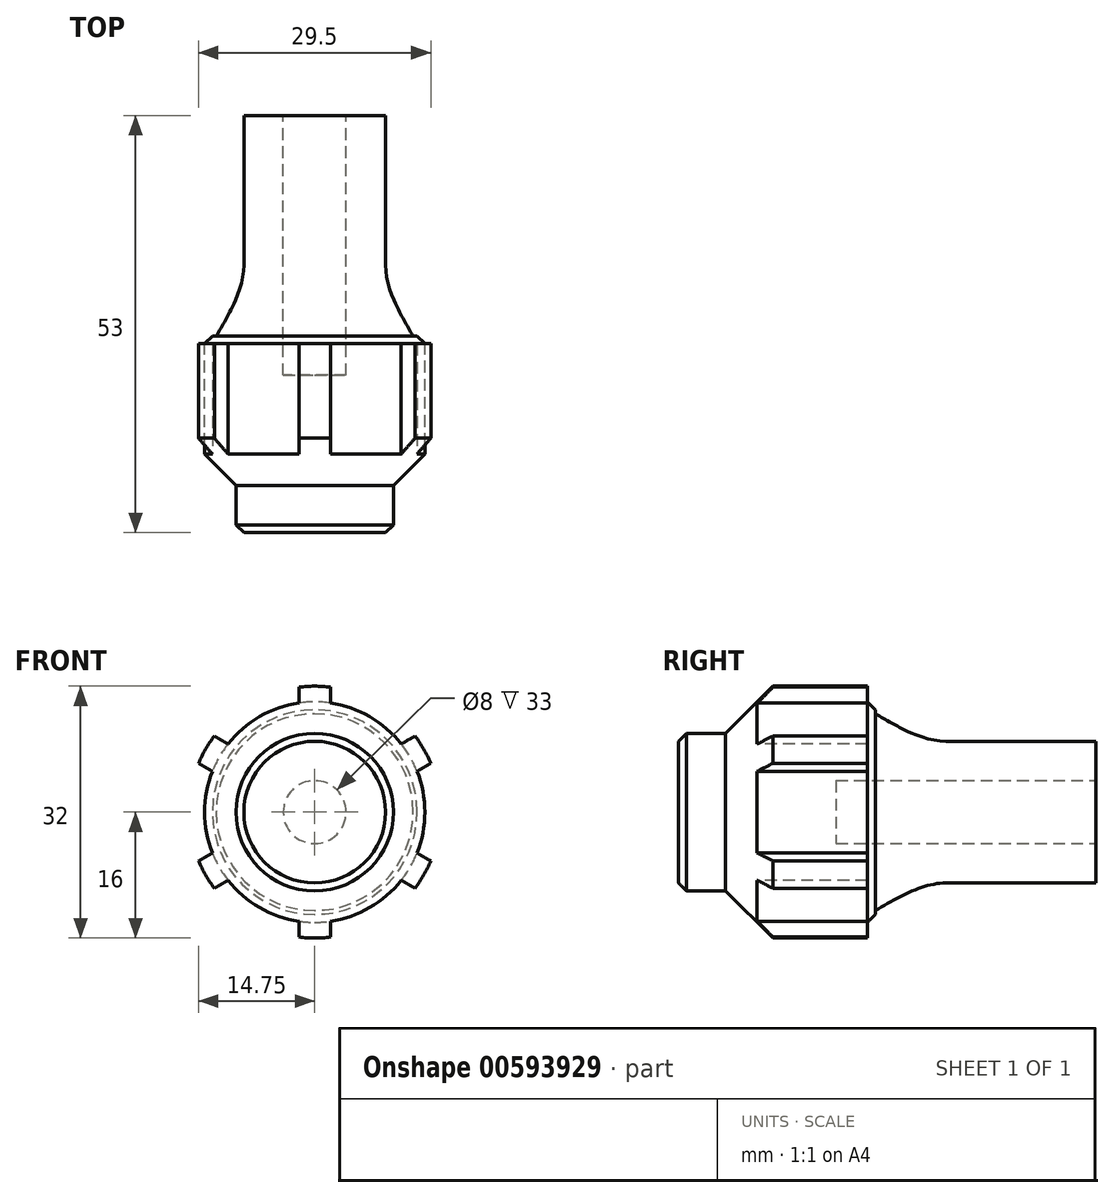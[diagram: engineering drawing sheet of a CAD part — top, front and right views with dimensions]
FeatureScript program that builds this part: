
annotation { "Feature Type Name" : "Feature", "Feature Type Description" : "" }
export const myFeature = defineFeature(function(context is Context, id is Id, definition is map)
    precondition{}
    {
        {
            var Q0;
            Q0=qCreatedBy(makeId("Front.planeOp"),FACE);
            var sketch = newSketch(context, id + "F0", { "sketchPlane" : qUnion([Q0])});
            skCircle(sketch, "E0", {"center": v(0, 0) * mm, "radius": 9 * mm});
            skSolve(sketch);
        }
        {
            var Q0;
            Q0=makeQuery(id+"F0.imprint","IMPRINT",FACE,{"disambiguationData":[TD([[makeQuery(id+"F0.imprint","IMPRINT",EDGE,{"derivedFrom":sQuery(id+"F0.wireOp",EDGE,"E0")}),1.0]])]});
            extrude(context, id + "F1", {"entities" : qUnion([Q0]), "depth" : 19 * mm, "offsetDistance" : 25 * mm});
        }
        {
            var Q0;
            Q0=makeQuery(id+"F1.opExtrude","CAP_FACE",FACE,{"disambiguationData":[OSD([sQuery(id+"F0.wireOp",EDGE,"E0")])],"isStart":false});
            cPlane(context, id + "F2", {"entities" : qUnion([Q0]), "cplaneType" : CPlaneType.OFFSET, "offset" : 9 * mm, "width" : 150 * mm, "height" : 150 * mm});
        }
        {
            var Q0;
            Q0=qCreatedBy(id+"F2.planeOp",FACE);
            var sketch = newSketch(context, id + "F3", { "sketchPlane" : qUnion([Q0])});
            skCircle(sketch, "E1", {"center": v(0, 0) * mm, "radius": 12.5 * mm});
            skSolve(sketch);
        }
        {
            var Q0;
            Q0=makeQuery(id+"F1.opExtrude","CAP_FACE",FACE,{"disambiguationData":[OSD([sQuery(id+"F0.wireOp",EDGE,"E0")])],"isStart":true});
            var sketch = newSketch(context, id + "F4", { "sketchPlane" : qUnion([Q0])});
            skCircle(sketch, "E2", {"center": v(0, 0) * mm, "radius": 4 * mm});
            skSolve(sketch);
        }
        {
            var Q1;
            Q1=makeQuery(id+"F1.opExtrude","CAP_FACE",FACE,{"disambiguationData":[OSD([sQuery(id+"F0.wireOp",EDGE,"E0")])],"isStart":false});
            var Q2;
            Q2=makeQuery(id+"F3.imprint","IMPRINT",FACE,{"disambiguationData":[TD([[makeQuery(id+"F3.imprint","IMPRINT",EDGE,{"derivedFrom":sQuery(id+"F3.wireOp",EDGE,"E1")}),1.0]])]});
            loft(context, id + "F5", {"operationType" : NewBodyOperationType.ADD, "startCondition" : LoftEndDerivativeType.NORMAL_TO_PROFILE, "startMagnitude" : 1, "sheetProfilesArray" : [{ "sheetProfileEntities" : qUnion([Q1]) }, { "sheetProfileEntities" : qUnion([Q2]) }]});
        }
        {
            var Q0;
            Q0=makeQuery(id+"F5.opLoft","CAP_FACE",FACE,{"disambiguationData":[OSD([makeQuery(id+"F3.imprint","IMPRINT",FACE,{"disambiguationData":[TD([[makeQuery(id+"F3.imprint","IMPRINT",EDGE,{"derivedFrom":sQuery(id+"F3.wireOp",EDGE,"E1")}),1.0]])]})])],"isStart":true});
            var sketch = newSketch(context, id + "F6", { "sketchPlane" : qUnion([Q0])});
            skCircle(sketch, "E3", {"center": v(0, 0) * mm, "radius": 14 * mm});
            skSolve(sketch);
        }
        {
            var Q0;
            Q0=makeQuery(id+"F6.imprint","IMPRINT",FACE,{"disambiguationData":[TD([[makeQuery(id+"F6.imprint","IMPRINT",EDGE,{"derivedFrom":makeQuery(id+"F5.opLoft","MID_CAP_EDGE",EDGE,{"disambiguationData":[OSD([sQuery(id+"F0.wireOp",EDGE,"E0"),sQuery(id+"F3.wireOp",EDGE,"E1")])],"capPos":1.0})}),1.0]])]});
            var Q1;
            Q1=makeQuery(id+"F6.imprint","IMPRINT",FACE,{"disambiguationData":[TD([[makeQuery(id+"F6.imprint","IMPRINT",EDGE,{"derivedFrom":sQuery(id+"F6.wireOp",EDGE,"E3")}),1.0]])]});
            extrude(context, id + "F7", {"entities" : qUnion([Q0, Q1]), "operationType" : NewBodyOperationType.ADD, "depth" : 19 * mm, "offsetDistance" : 25 * mm});
        }
        {
            var Q0;
            Q0=makeQuery(id+"F7.opExtrude","CAP_FACE",FACE,{"disambiguationData":[OSD([sQuery(id+"F6.wireOp",EDGE,"E3")])],"isStart":false});
            var sketch = newSketch(context, id + "F8", { "sketchPlane" : qUnion([Q0])});
            skCircle(sketch, "E4", {"center": v(0, 0) * mm, "radius": 10 * mm});
            skSolve(sketch);
        }
        {
            var Q0;
            Q0 = qSketchRegion(id + "F8", true);
            extrude(context, id + "F9", {"entities" : qUnion([Q0]), "operationType" : NewBodyOperationType.ADD, "depth" : 6 * mm, "offsetDistance" : 25 * mm});
        }
        {
            var Q0;
            Q0=makeQuery(id+"F7.opExtrude","CAP_EDGE",EDGE,{"disambiguationData":[OSD([sQuery(id+"F6.wireOp",EDGE,"E3")])],"isStart":false});
            chamfer(context, id + "F10", {"entities" : qUnion([Q0]), "width" : 4 * mm, "tangentPropagation" : true});
        }
        {
            var Q0;
            Q0=makeQuery(id+"F7.opExtrude","CAP_EDGE",EDGE,{"disambiguationData":[OSD([sQuery(id+"F6.wireOp",EDGE,"E3")])],"isStart":true});
            var Q1;
            Q1=makeQuery(id+"F9.opExtrude","CAP_EDGE",EDGE,{"disambiguationData":[OSD([sQuery(id+"F8.wireOp",EDGE,"E4")])],"isStart":false});
            chamfer(context, id + "F11", {"entities" : qUnion([Q0, Q1]), "width" : 1 * mm, "tangentPropagation" : true});
        }
        {
            var Q0;
            Q0=qCreatedBy(makeId("Front.planeOp"),FACE);
            cPlane(context, id + "F12", {"entities" : qUnion([Q0]), "cplaneType" : CPlaneType.OFFSET, "offset" : 43 * mm, "width" : 150 * mm, "height" : 150 * mm});
        }
        {
            var Q0;
            Q0=qCreatedBy(id+"F12.planeOp",FACE);
            var sketch = newSketch(context, id + "F13", { "sketchPlane" : qUnion([Q0])});
            skArc(sketch, "E5.0", {"start": v(2, 13.86) * mm, "mid": v(0, 14) * mm, "end": v(-2, 13.86) * mm});
            skLineSegment(sketch, "E6", {"start": v(-2, 13.86) * mm, "end": v(-2, 15.87) * mm});
            skLineSegment(sketch, "E7.MirrorCS", {"start": v(2, 13.86) * mm, "end": v(2, 15.87) * mm});
            skArc(sketch, "E8", {"start": v(-2, 15.87) * mm, "mid": v(0, 16) * mm, "end": v(2, 15.87) * mm});
            skArc(sketch, "E9.1.0", {"start": v(-11, 8.66) * mm, "mid": v(-12.12, 7) * mm, "end": v(-13, 5.2) * mm});
            skLineSegment(sketch, "E9.1.1", {"start": v(-11, 8.66) * mm, "end": v(-12.75, 9.67) * mm});
            skArc(sketch, "E9.1.2", {"start": v(-14.75, 6.2) * mm, "mid": v(-13.86, 8) * mm, "end": v(-12.75, 9.67) * mm});
            skLineSegment(sketch, "E9.1.3", {"start": v(-13, 5.2) * mm, "end": v(-14.75, 6.2) * mm});
            skArc(sketch, "E9.2.0", {"start": v(-13, -5.2) * mm, "mid": v(-12.12, -7) * mm, "end": v(-11, -8.66) * mm});
            skLineSegment(sketch, "E9.2.1", {"start": v(-13, -5.2) * mm, "end": v(-14.75, -6.2) * mm});
            skArc(sketch, "E9.2.2", {"start": v(-12.75, -9.67) * mm, "mid": v(-13.86, -8) * mm, "end": v(-14.75, -6.2) * mm});
            skLineSegment(sketch, "E9.2.3", {"start": v(-11, -8.66) * mm, "end": v(-12.75, -9.67) * mm});
            skArc(sketch, "E9.3.0", {"start": v(-2, -13.86) * mm, "mid": v(0, -14) * mm, "end": v(2, -13.86) * mm});
            skLineSegment(sketch, "E9.3.1", {"start": v(-2, -13.86) * mm, "end": v(-2, -15.87) * mm});
            skArc(sketch, "E9.3.2", {"start": v(2, -15.87) * mm, "mid": v(0, -16) * mm, "end": v(-2, -15.87) * mm});
            skLineSegment(sketch, "E9.3.3", {"start": v(2, -13.86) * mm, "end": v(2, -15.87) * mm});
            skArc(sketch, "E9.4.0", {"start": v(11, -8.66) * mm, "mid": v(12.12, -7) * mm, "end": v(13, -5.2) * mm});
            skLineSegment(sketch, "E9.4.1", {"start": v(11, -8.66) * mm, "end": v(12.75, -9.67) * mm});
            skArc(sketch, "E9.4.2", {"start": v(14.75, -6.2) * mm, "mid": v(13.86, -8) * mm, "end": v(12.75, -9.67) * mm});
            skLineSegment(sketch, "E9.4.3", {"start": v(13, -5.2) * mm, "end": v(14.75, -6.2) * mm});
            skArc(sketch, "E9.5.0", {"start": v(13, 5.2) * mm, "mid": v(12.12, 7) * mm, "end": v(11, 8.66) * mm});
            skLineSegment(sketch, "E9.5.1", {"start": v(13, 5.2) * mm, "end": v(14.75, 6.2) * mm});
            skArc(sketch, "E9.5.2", {"start": v(12.75, 9.67) * mm, "mid": v(13.86, 8) * mm, "end": v(14.75, 6.2) * mm});
            skLineSegment(sketch, "E9.5.3", {"start": v(11, 8.66) * mm, "end": v(12.75, 9.67) * mm});
            skSolve(sketch);
        }
        {
            var Q0;
            Q0=makeQuery(id+"F13.imprint","IMPRINT",FACE,{"disambiguationData":[TD([[makeQuery(id+"F13.imprint","IMPRINT",EDGE,{"derivedFrom":sQuery(id+"F13.wireOp",EDGE,"E5.0")}),-1.0]])]});
            var Q1;
            Q1=makeQuery(id+"F13.imprint","IMPRINT",FACE,{"disambiguationData":[TD([[makeQuery(id+"F13.imprint","IMPRINT",EDGE,{"derivedFrom":sQuery(id+"F13.wireOp",EDGE,"E9.1.0")}),-1.0]])]});
            var Q2;
            Q2=makeQuery(id+"F13.imprint","IMPRINT",FACE,{"disambiguationData":[TD([[makeQuery(id+"F13.imprint","IMPRINT",EDGE,{"derivedFrom":sQuery(id+"F13.wireOp",EDGE,"E9.2.0")}),-1.0]])]});
            var Q3;
            Q3=makeQuery(id+"F13.imprint","IMPRINT",FACE,{"disambiguationData":[TD([[makeQuery(id+"F13.imprint","IMPRINT",EDGE,{"derivedFrom":sQuery(id+"F13.wireOp",EDGE,"E9.4.0")}),-1.0]])]});
            var Q4;
            Q4=makeQuery(id+"F13.imprint","IMPRINT",FACE,{"disambiguationData":[TD([[makeQuery(id+"F13.imprint","IMPRINT",EDGE,{"derivedFrom":sQuery(id+"F13.wireOp",EDGE,"E9.5.0")}),-1.0]])]});
            var Q5;
            Q5=makeQuery(id+"F13.imprint","IMPRINT",FACE,{"disambiguationData":[TD([[makeQuery(id+"F13.imprint","IMPRINT",EDGE,{"derivedFrom":sQuery(id+"F13.wireOp",EDGE,"E9.5.0")}),-1.0]])]});
            var Q6;
            Q6=makeQuery(id+"F13.imprint","IMPRINT",FACE,{"disambiguationData":[TD([[makeQuery(id+"F13.imprint","IMPRINT",EDGE,{"derivedFrom":sQuery(id+"F13.wireOp",EDGE,"E9.3.0")}),-1.0]])]});
            var Q7;
            Q7=makeQuery(id+"F7.opExtrude","CAP_FACE",FACE,{"disambiguationData":[OSD([sQuery(id+"F6.wireOp",EDGE,"E3")])],"isStart":true});
            extrude(context, id + "F14", {"entities" : qUnion([Q0, Q1, Q2, Q3, Q4, Q5, Q6]), "operationType" : NewBodyOperationType.ADD, "endBound" : BoundingType.UP_TO_SURFACE, "oppositeDirection" : true, "depth" : 25 * mm, "endBoundEntityFace" : qUnion([Q7]), "hasOffset" : true, "offsetDistance" : 1 * mm});
        }
        {
            var Q0;
            Q0=makeQuery(id+"F14.opExtrude","CAP_EDGE",EDGE,{"disambiguationData":[OSD([sQuery(id+"F13.wireOp",EDGE,"E9.1.2")])],"isStart":true});
            var Q1;
            Q1=makeQuery(id+"F14.opExtrude","CAP_EDGE",EDGE,{"disambiguationData":[OSD([sQuery(id+"F13.wireOp",EDGE,"E9.2.2")])],"isStart":true});
            var Q2;
            Q2=makeQuery(id+"F14.opExtrude","CAP_EDGE",EDGE,{"disambiguationData":[OSD([sQuery(id+"F13.wireOp",EDGE,"E8")])],"isStart":true});
            var Q3;
            Q3=makeQuery(id+"F14.opExtrude","CAP_EDGE",EDGE,{"disambiguationData":[OSD([sQuery(id+"F13.wireOp",EDGE,"E9.5.2")])],"isStart":true});
            var Q4;
            Q4=makeQuery(id+"F14.opExtrude","CAP_EDGE",EDGE,{"disambiguationData":[OSD([sQuery(id+"F13.wireOp",EDGE,"E9.4.2")])],"isStart":true});
            var Q5;
            Q5=makeQuery(id+"F14.opExtrude","CAP_EDGE",EDGE,{"disambiguationData":[OSD([sQuery(id+"F13.wireOp",EDGE,"E9.3.2")])],"isStart":true});
            var Q6;
            Q6=makeQuery(id+"F14.opExtrude","TWEAK_EDGE",EDGE,{"derivedFrom":[makeQuery(id+"F7.opExtrude","CAP_FACE",FACE,{"disambiguationData":[OSD([sQuery(id+"F6.wireOp",EDGE,"E3")])],"isStart":true}),makeQuery(id+"F13.imprint","IMPRINT",EDGE,{"derivedFrom":sQuery(id+"F13.wireOp",EDGE,"E8")})]});
            var Q7;
            Q7=makeQuery(id+"F14.opExtrude","TWEAK_EDGE",EDGE,{"derivedFrom":[makeQuery(id+"F7.opExtrude","CAP_FACE",FACE,{"disambiguationData":[OSD([sQuery(id+"F6.wireOp",EDGE,"E3")])],"isStart":true}),makeQuery(id+"F13.imprint","IMPRINT",EDGE,{"derivedFrom":sQuery(id+"F13.wireOp",EDGE,"E9.5.2")})]});
            var Q8;
            Q8=makeQuery(id+"F14.opExtrude","TWEAK_EDGE",EDGE,{"derivedFrom":[makeQuery(id+"F7.opExtrude","CAP_FACE",FACE,{"disambiguationData":[OSD([sQuery(id+"F6.wireOp",EDGE,"E3")])],"isStart":true}),makeQuery(id+"F13.imprint","IMPRINT",EDGE,{"derivedFrom":sQuery(id+"F13.wireOp",EDGE,"E9.1.2")})]});
            var Q9;
            Q9=makeQuery(id+"F14.opExtrude","TWEAK_EDGE",EDGE,{"derivedFrom":[makeQuery(id+"F7.opExtrude","CAP_FACE",FACE,{"disambiguationData":[OSD([sQuery(id+"F6.wireOp",EDGE,"E3")])],"isStart":true}),makeQuery(id+"F13.imprint","IMPRINT",EDGE,{"derivedFrom":sQuery(id+"F13.wireOp",EDGE,"E9.2.2")})]});
            var Q10;
            Q10=makeQuery(id+"F14.opExtrude","TWEAK_EDGE",EDGE,{"derivedFrom":[makeQuery(id+"F7.opExtrude","CAP_FACE",FACE,{"disambiguationData":[OSD([sQuery(id+"F6.wireOp",EDGE,"E3")])],"isStart":true}),makeQuery(id+"F13.imprint","IMPRINT",EDGE,{"derivedFrom":sQuery(id+"F13.wireOp",EDGE,"E9.3.2")})]});
            var Q11;
            Q11=makeQuery(id+"F14.opExtrude","TWEAK_EDGE",EDGE,{"derivedFrom":[makeQuery(id+"F7.opExtrude","CAP_FACE",FACE,{"disambiguationData":[OSD([sQuery(id+"F6.wireOp",EDGE,"E3")])],"isStart":true}),makeQuery(id+"F13.imprint","IMPRINT",EDGE,{"derivedFrom":sQuery(id+"F13.wireOp",EDGE,"E9.4.2")})]});
            chamfer(context, id + "F15", {"entities" : qUnion([Q0, Q1, Q2, Q3, Q4, Q5, Q6, Q7, Q8, Q9, Q10, Q11]), "width" : 2 * mm, "tangentPropagation" : true});
        }
        {
            var Q0;
            Q0=makeQuery(id+"F4.imprint","IMPRINT",FACE,{"disambiguationData":[TD([[makeQuery(id+"F4.imprint","IMPRINT",EDGE,{"derivedFrom":sQuery(id+"F4.wireOp",EDGE,"E2")}),1.0]])]});
            extrude(context, id + "F16", {"entities" : qUnion([Q0]), "operationType" : NewBodyOperationType.REMOVE, "oppositeDirection" : true, "depth" : 33 * mm, "offsetDistance" : 25 * mm});
        }
    });
